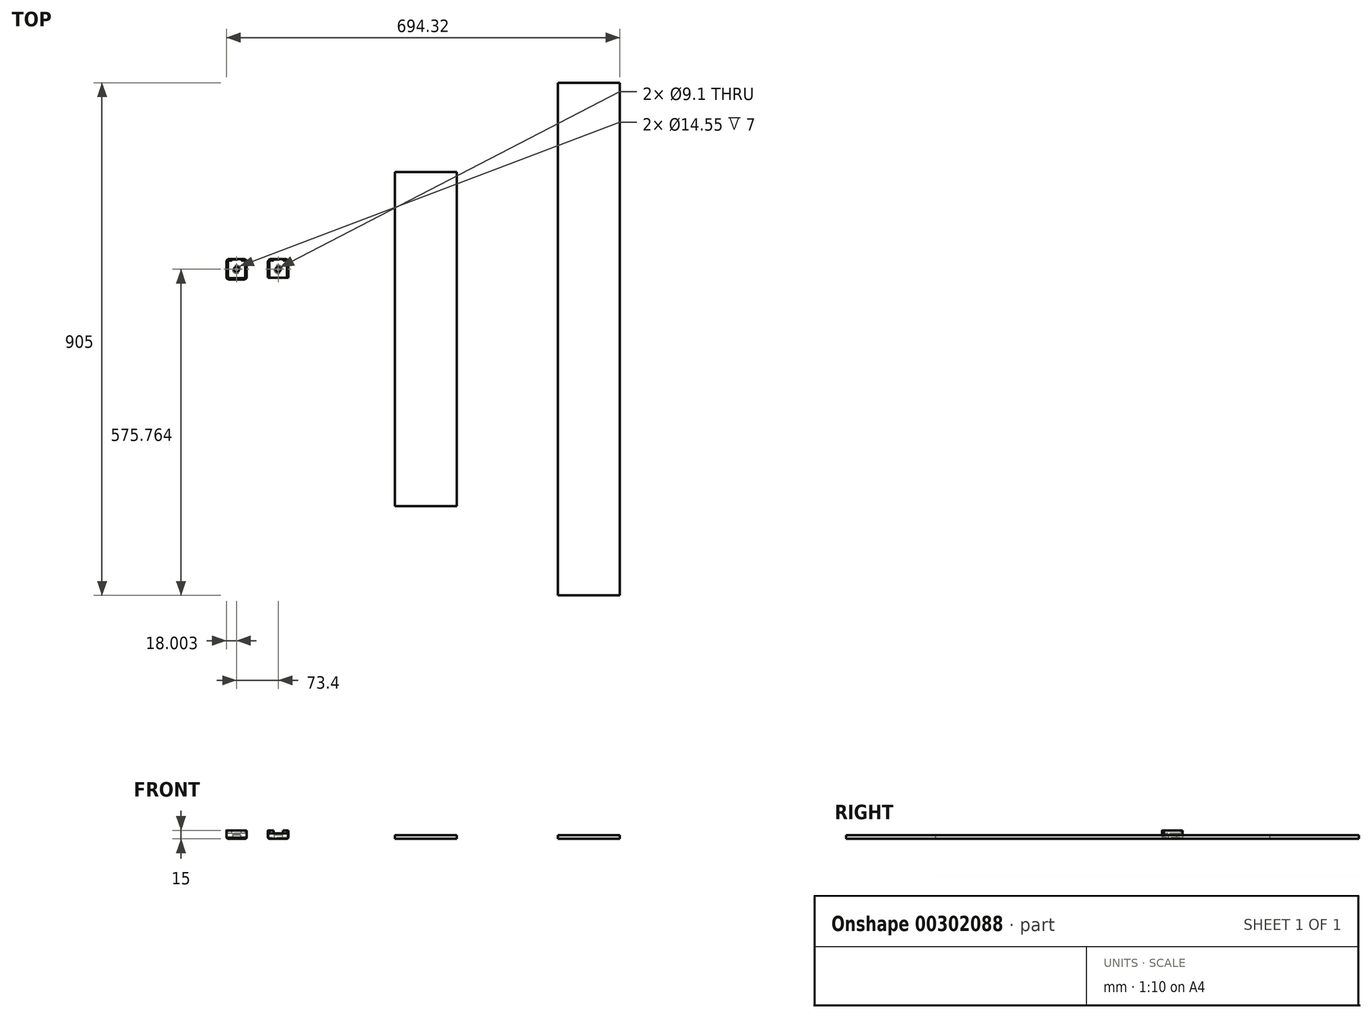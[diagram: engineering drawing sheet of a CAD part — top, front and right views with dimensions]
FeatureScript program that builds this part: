
annotation { "Feature Type Name" : "Feature", "Feature Type Description" : "" }
export const myFeature = defineFeature(function(context is Context, id is Id, definition is map)
    precondition{}
    {
        {
            var Q0;
            Q0=qCreatedBy(makeId("Top.planeOp"),FACE);
            var sketch = newSketch(context, id + "F0", { "sketchPlane" : qUnion([Q0])});
            skLineSegment(sketch, "E0.bottom", {"start": v(-54.5, 295) * mm, "end": v(54.5, 295) * mm});
            skLineSegment(sketch, "E0.top", {"start": v(-54.5, -295) * mm, "end": v(54.5, -295) * mm});
            skLineSegment(sketch, "E0.left", {"start": v(-54.5, 295) * mm, "end": v(-54.5, -295) * mm});
            skLineSegment(sketch, "E0.right", {"start": v(54.5, 295) * mm, "end": v(54.5, -295) * mm});
            skPoint(sketch, "E0.middle", {"position": v(0, 0) * mm});
            skLineSegment(sketch, "E1.bottom", {"start": v(233.4, 452.5) * mm, "end": v(342.4, 452.5) * mm});
            skLineSegment(sketch, "E1.top", {"start": v(233.4, -452.5) * mm, "end": v(342.4, -452.5) * mm});
            skLineSegment(sketch, "E1.left", {"start": v(233.4, 452.5) * mm, "end": v(233.4, -452.5) * mm});
            skLineSegment(sketch, "E1.right", {"start": v(342.4, 452.5) * mm, "end": v(342.4, -452.5) * mm});
            skPoint(sketch, "E1.middle", {"position": v(287.9, 0) * mm});
            skLineSegment(sketch, "E2.bottom", {"start": v(-351.92, 141.26) * mm, "end": v(-315.92, 141.26) * mm});
            skLineSegment(sketch, "E2.top", {"start": v(-351.92, 105.26) * mm, "end": v(-315.92, 105.26) * mm});
            skLineSegment(sketch, "E2.left", {"start": v(-351.92, 141.26) * mm, "end": v(-351.92, 105.26) * mm});
            skLineSegment(sketch, "E2.right", {"start": v(-315.92, 141.26) * mm, "end": v(-315.92, 105.26) * mm});
            skPoint(sketch, "E2.middle", {"position": v(-333.92, 123.26) * mm});
            skSolve(sketch);
        }
        {
            var Q0;
            Q0=makeQuery(id+"F0.imprint","IMPRINT",FACE,{"disambiguationData":[TD([[makeQuery(id+"F0.imprint","IMPRINT",EDGE,{"derivedFrom":sQuery(id+"F0.wireOp",EDGE,"E0.bottom")}),-1.0]])]});
            var Q1;
            Q1=makeQuery(id+"F0.imprint","IMPRINT",FACE,{"disambiguationData":[TD([[makeQuery(id+"F0.imprint","IMPRINT",EDGE,{"derivedFrom":sQuery(id+"F0.wireOp",EDGE,"E1.bottom")}),-1.0]])]});
            extrude(context, id + "F1", {"entities" : qUnion([Q0, Q1]), "depth" : 6.35 * mm});
        }
        {
            var Q0;
            Q0=makeQuery(id+"F0.imprint","IMPRINT",FACE,{"disambiguationData":[TD([[makeQuery(id+"F0.imprint","IMPRINT",EDGE,{"derivedFrom":sQuery(id+"F0.wireOp",EDGE,"E2.bottom")}),-1.0]])]});
            extrude(context, id + "F2", {"entities" : qUnion([Q0]), "depth" : 15 * mm});
        }
        {
            var Q0;
            Q0=makeQuery(id+"F2.opExtrude","CAP_FACE",FACE,{"disambiguationData":[OSD([sQuery(id+"F0.wireOp",EDGE,"E2.bottom"),sQuery(id+"F0.wireOp",EDGE,"E2.top"),sQuery(id+"F0.wireOp",EDGE,"E2.left"),sQuery(id+"F0.wireOp",EDGE,"E2.right")])],"isStart":false});
            var sketch = newSketch(context, id + "F3", { "sketchPlane" : qUnion([Q0])});
            skLineSegment(sketch, "E3.bottom", {"start": v(-318.42, 138.76) * mm, "end": v(-349.42, 138.76) * mm});
            skLineSegment(sketch, "E3.top", {"start": v(-318.42, 107.76) * mm, "end": v(-349.42, 107.76) * mm});
            skLineSegment(sketch, "E3.left", {"start": v(-318.42, 138.76) * mm, "end": v(-318.42, 107.76) * mm});
            skLineSegment(sketch, "E3.right", {"start": v(-349.42, 138.76) * mm, "end": v(-349.42, 107.76) * mm});
            skPoint(sketch, "E3.middle", {"position": v(-333.92, 123.26) * mm});
            skPoint(sketch, "E3.middle.positionSnap0", {"position": v(-351.92, 123.26) * mm});
            skPoint(sketch, "E3.middle.positionSnap1", {"position": v(-333.92, 141.26) * mm});
            skPoint(sketch, "E3.centerSnap0", {"position": v(-351.92, 123.26) * mm});
            skPoint(sketch, "E3.centerSnap1", {"position": v(-333.92, 141.26) * mm});
            skSolve(sketch);
        }
        {
            var Q0;
            Q0=makeQuery(id+"F3.imprint","IMPRINT",FACE,{"disambiguationData":[TD([[makeQuery(id+"F3.imprint","IMPRINT",EDGE,{"derivedFrom":sQuery(id+"F3.wireOp",EDGE,"E3.bottom")}),1.0]])]});
            extrude(context, id + "F4", {"entities" : qUnion([Q0]), "operationType" : NewBodyOperationType.REMOVE, "oppositeDirection" : true, "depth" : 5 * mm});
        }
        {
            var Q0;
            Q0=makeQuery(id+"F2.opExtrude","CAP_FACE",FACE,{"disambiguationData":[OSD([sQuery(id+"F0.wireOp",EDGE,"E2.bottom"),sQuery(id+"F0.wireOp",EDGE,"E2.top"),sQuery(id+"F0.wireOp",EDGE,"E2.left"),sQuery(id+"F0.wireOp",EDGE,"E2.right")])],"isStart":false});
            var sketch = newSketch(context, id + "F5", { "sketchPlane" : qUnion([Q0])});
            skLineSegment(sketch, "E4.bottom", {"start": v(-342.17, 141.26) * mm, "end": v(-325.67, 141.26) * mm});
            skLineSegment(sketch, "E4.top", {"start": v(-342.17, 138.76) * mm, "end": v(-325.67, 138.76) * mm});
            skLineSegment(sketch, "E4.left", {"start": v(-342.17, 141.26) * mm, "end": v(-342.17, 138.76) * mm});
            skLineSegment(sketch, "E4.right", {"start": v(-325.67, 141.26) * mm, "end": v(-325.67, 138.76) * mm});
            skPoint(sketch, "E5", {"position": v(-333.92, 141.26) * mm});
            skSolve(sketch);
        }
        {
            var Q0;
            Q0 = qSketchRegion(id + "F5", true);
            extrude(context, id + "F6", {"entities" : qUnion([Q0]), "operationType" : NewBodyOperationType.REMOVE, "oppositeDirection" : true, "depth" : 5 * mm});
        }
        {
            var Q0;
            Q0=sQuery(id+"F0.wireOp",VERTEX,"E2.middle");
            var Q1;
            Q1=makeQuery(id+"F2.opExtrude","SWEPT_BODY",BODY,{"disambiguationData":[OSD([sQuery(id+"F0.wireOp",EDGE,"E2.bottom"),sQuery(id+"F0.wireOp",EDGE,"E2.top"),sQuery(id+"F0.wireOp",EDGE,"E2.left"),sQuery(id+"F0.wireOp",EDGE,"E2.right")])]});
            hole(context, id + "F7", {"style" : HoleStyle.C_BORE, "endStyle" : HoleEndStyle.THROUGH, "oppositeDirection" : true, "holeDiameter" : 9.1 * mm, "cBoreDiameter" : 14.55 * mm, "cBoreDepth" : 7 * mm, "tappedDepth" : 12 * mm, "tapClearance" : 3, "locations" : qUnion([Q0]), "scope" : qUnion([Q1])});
        }
        {
            var Q0;
            Q0=makeQuery(id+"F2.opExtrude","SWEPT_EDGE",EDGE,{"disambiguationData":[OSD([sQuery(id+"F0.wireOp",EDGE,"E2.bottom"),sQuery(id+"F0.wireOp",EDGE,"E2.left")])]});
            var Q1;
            Q1=makeQuery(id+"F2.opExtrude","SWEPT_EDGE",EDGE,{"disambiguationData":[OSD([sQuery(id+"F0.wireOp",EDGE,"E2.top"),sQuery(id+"F0.wireOp",EDGE,"E2.left")])]});
            var Q2;
            Q2=makeQuery(id+"F2.opExtrude","SWEPT_EDGE",EDGE,{"disambiguationData":[OSD([sQuery(id+"F0.wireOp",EDGE,"E2.bottom"),sQuery(id+"F0.wireOp",EDGE,"E2.right")])]});
            var Q3;
            Q3=makeQuery(id+"F2.opExtrude","SWEPT_EDGE",EDGE,{"disambiguationData":[OSD([sQuery(id+"F0.wireOp",EDGE,"E2.top"),sQuery(id+"F0.wireOp",EDGE,"E2.right")])]});
            fillet(context, id + "F8", {"entities" : qUnion([Q0, Q1, Q2, Q3]), "radius" : 5 * mm, "tangentPropagation" : true, "allowEdgeOverflow" : false});
        }
        {
            var Q0;
            Q0=makeQuery(id+"F2.opExtrude","CAP_EDGE",EDGE,{"disambiguationData":[OSD([sQuery(id+"F0.wireOp",EDGE,"E2.top")])],"isStart":true});
            chamfer(context, id + "F9", {"entities" : qUnion([Q0]), "width" : 2 * mm, "tangentPropagation" : true});
        }
        {
            var Q0;
            Q0=makeQuery(id+"F2.opExtrude","SWEPT_BODY",BODY,{"disambiguationData":[OSD([sQuery(id+"F0.wireOp",EDGE,"E2.bottom"),sQuery(id+"F0.wireOp",EDGE,"E2.top"),sQuery(id+"F0.wireOp",EDGE,"E2.left"),sQuery(id+"F0.wireOp",EDGE,"E2.right")])]});
            transform(context, id + "F10", {"entities" : qUnion([Q0]), "transformType" : TransformType.TRANSLATION_3D, "dx" : 73.4 * mm, "dy" : 0 * mm, "dz" : 0 * mm, "makeCopy" : true});
        }
        {
            var Q0;
            Q0=makeQuery(id+"F10.opPattern","COPY",FACE,{"derivedFrom":makeQuery(id+"F4.boolean.opBoolean","COPY",FACE,{"derivedFrom":makeQuery(id+"F4.opExtrude","SWEPT_FACE",FACE,{"disambiguationData":[OSD([sQuery(id+"F3.wireOp",EDGE,"E3.top")])]})}),"instanceName":"1"});
            var sketch = newSketch(context, id + "F11", { "sketchPlane" : qUnion([Q0])});
            skLineSegment(sketch, "E6.0", {"start": v(245.02, 15) * mm, "end": v(276.02, 15) * mm});
            skLineSegment(sketch, "E7.0", {"start": v(245.02, 10) * mm, "end": v(276.02, 10) * mm});
            skLineSegment(sketch, "E8.0", {"start": v(245.02, 10) * mm, "end": v(245.02, 15) * mm});
            skSolve(sketch);
        }
        {
            var Q0;
            Q0=makeQuery(id+"F11.imprint","IMPRINT",FACE,{"disambiguationData":[TD([[makeQuery(id+"F11.imprint","IMPRINT",EDGE,{"derivedFrom":sQuery(id+"F11.wireOp",EDGE,"E6.0")}),-1.0]])]});
            extrude(context, id + "F12", {"entities" : qUnion([Q0]), "operationType" : NewBodyOperationType.REMOVE, "oppositeDirection" : true, "depth" : 25 * mm});
        }
        {
            var Q0;
            Q0=makeQuery(id+"F12.boolean.opBoolean","INTERSECT",EDGE,{"derivedFrom":[makeQuery(id+"F10.opPattern","COPY",FACE,{"derivedFrom":makeQuery(id+"F8.opFillet","BLEND_FACE",FACE,{"disambiguationData":[OSD([sQuery(id+"F0.wireOp",EDGE,"E2.top"),sQuery(id+"F0.wireOp",EDGE,"E2.right")])]}),"instanceName":"1"}),makeQuery(id+"F12.opExtrude","SWEPT_FACE",FACE,{"disambiguationData":[OSD([sQuery(id+"F11.wireOp",EDGE,"E8.0")])]})]});
            var Q1;
            Q1=makeQuery(id+"F12.boolean.opBoolean","INTERSECT",EDGE,{"derivedFrom":[makeQuery(id+"F10.opPattern","COPY",FACE,{"derivedFrom":makeQuery(id+"F8.opFillet","BLEND_FACE",FACE,{"disambiguationData":[OSD([sQuery(id+"F0.wireOp",EDGE,"E2.top"),sQuery(id+"F0.wireOp",EDGE,"E2.left")])]}),"instanceName":"1"}),makeQuery(id+"F12.opExtrude","SWEPT_FACE",FACE,{"disambiguationData":[OSD([sQuery(id+"F3.wireOp",EDGE,"E3.top"),sQuery(id+"F3.wireOp",EDGE,"E3.right")])]})]});
            fillet(context, id + "F13", {"entities" : qUnion([Q0, Q1]), "radius" : 0.5 * mm, "tangentPropagation" : true, "allowEdgeOverflow" : false});
        }
        {
            var Q0;
            Q0=makeQuery(id+"F12.boolean.opBoolean","MERGE",FACE,{"derivedFrom":[makeQuery(id+"F10.opPattern","COPY",FACE,{"derivedFrom":makeQuery(id+"F6.boolean.opBoolean","MERGE",FACE,{"derivedFrom":[makeQuery(id+"F4.boolean.opBoolean","COPY",FACE,{"derivedFrom":makeQuery(id+"F4.opExtrude","CAP_FACE",FACE,{"disambiguationData":[OSD([sQuery(id+"F3.wireOp",EDGE,"E3.bottom"),sQuery(id+"F3.wireOp",EDGE,"E3.top"),sQuery(id+"F3.wireOp",EDGE,"E3.left"),sQuery(id+"F3.wireOp",EDGE,"E3.right")])],"isStart":false})}),makeQuery(id+"F6.opExtrude","CAP_FACE",FACE,{"disambiguationData":[OSD([sQuery(id+"F5.wireOp",EDGE,"E4.bottom"),sQuery(id+"F5.wireOp",EDGE,"E4.top"),sQuery(id+"F5.wireOp",EDGE,"E4.left"),sQuery(id+"F5.wireOp",EDGE,"E4.right")])],"isStart":false})]}),"instanceName":"1"}),makeQuery(id+"F12.opExtrude","SWEPT_FACE",FACE,{"disambiguationData":[OSD([sQuery(id+"F11.wireOp",EDGE,"E7.0")])]})]});
            var sketch = newSketch(context, id + "F14", { "sketchPlane" : qUnion([Q0])});
            skCircle(sketch, "E9.0", {"center": v(-260.52, 123.26) * mm, "radius": 4.55 * mm});
            skLineSegment(sketch, "E10.bottom", {"start": v(-275.52, 138.26) * mm, "end": v(-245.52, 138.26) * mm, "construction": true});
            skLineSegment(sketch, "E10.top", {"start": v(-275.52, 108.26) * mm, "end": v(-245.52, 108.26) * mm, "construction": true});
            skLineSegment(sketch, "E10.left", {"start": v(-275.52, 138.26) * mm, "end": v(-275.52, 108.26) * mm, "construction": true});
            skLineSegment(sketch, "E10.right", {"start": v(-245.52, 138.26) * mm, "end": v(-245.52, 108.26) * mm, "construction": true});
            skLineSegment(sketch, "E11.0", {"start": v(-247.52, 105.26) * mm, "end": v(-273.52, 105.26) * mm});
            skArc(sketch, "E12.0", {"start": v(-247.52, 105.26) * mm, "mid": v(-245.73, 105.6) * mm, "end": v(-244.18, 106.54) * mm});
            skArc(sketch, "E13.0", {"start": v(-244.18, 106.54) * mm, "mid": v(-243.47, 107.33) * mm, "end": v(-242.93, 108.26) * mm});
            skArc(sketch, "E14.0", {"start": v(-276.85, 106.54) * mm, "mid": v(-275.3, 105.6) * mm, "end": v(-273.52, 105.26) * mm});
            skArc(sketch, "E15.0", {"start": v(-278.1, 108.26) * mm, "mid": v(-276.26, 106.08) * mm, "end": v(-273.52, 105.26) * mm});
            skLineSegment(sketch, "E16", {"start": v(-278.1, 108.26) * mm, "end": v(-242.93, 108.26) * mm});
            skPoint(sketch, "E17.orphan", {"position": v(-278.52, 110.26) * mm});
            skPoint(sketch, "E18.orphan", {"position": v(-242.52, 110.26) * mm});
            skSolve(sketch);
        }
        {
            var Q0;
            {var subQ1=sQuery(id+"F3.wireOp",EDGE,"E3.left");var subQ2=makeQuery(id+"F4.boolean.opBoolean","COPY",FACE,{"derivedFrom":makeQuery(id+"F4.opExtrude","SWEPT_FACE",FACE,{"disambiguationData":[OSD([subQ1])]})});var subQ4=sQuery(id+"F0.wireOp",EDGE,"E2.right");var subQ5=sQuery(id+"F0.wireOp",EDGE,"E2.top");var subQ6=sQuery(id+"F0.wireOp",EDGE,"E2.bottom");var subQ7=makeQuery(id+"F2.opExtrude","CAP_FACE",FACE,{"disambiguationData":[OSD([subQ6,subQ5,sQuery(id+"F0.wireOp",EDGE,"E2.left"),subQ4])],"isStart":false});Q0=makeQuery(id+"F12.boolean.opBoolean","SPLIT",FACE,{"disambiguationData":[TD([makeQuery(id+"F10.opPattern","COPY",FACE,{"derivedFrom":subQ2,"instanceName":"1"})])],"derivedFrom":makeQuery(id+"F10.opPattern","COPY",FACE,{"derivedFrom":subQ7,"instanceName":"1"})});}
            var sketch = newSketch(context, id + "F15", { "sketchPlane" : qUnion([Q0])});
            skLineSegment(sketch, "E19.0", {"start": v(-278.1, 108.26) * mm, "end": v(-242.93, 108.26) * mm});
            skArc(sketch, "E20.0", {"start": v(-278.1, 108.26) * mm, "mid": v(-276.26, 106.08) * mm, "end": v(-273.52, 105.26) * mm});
            skLineSegment(sketch, "E21.0", {"start": v(-247.52, 105.26) * mm, "end": v(-273.52, 105.26) * mm});
            skArc(sketch, "E22.0", {"start": v(-247.52, 105.26) * mm, "mid": v(-245.73, 105.6) * mm, "end": v(-244.18, 106.54) * mm});
            skArc(sketch, "E23.0", {"start": v(-244.18, 106.54) * mm, "mid": v(-243.47, 107.33) * mm, "end": v(-242.93, 108.26) * mm});
            skSolve(sketch);
        }
        {
            var Q0;
            {var subQ16=sQuery(id+"F15.wireOp",EDGE,"E20.0");Q0=makeQuery(id+"F15.imprint","IMPRINT",FACE,{"disambiguationData":[TD([[makeQuery(id+"F15.imprint","IMPRINT",EDGE,{"derivedFrom":subQ16}),1.0]])]});}
            var Q1;
            {var subQ0=sQuery(id+"F15.wireOp",EDGE,"E23.0");Q1=makeQuery(id+"F15.imprint","IMPRINT",FACE,{"disambiguationData":[TD([[makeQuery(id+"F15.imprint","IMPRINT",EDGE,{"derivedFrom":subQ0}),1.0]])]});}
            var Q2;
            Q2=makeQuery(id+"F10.opPattern","COPY",FACE,{"derivedFrom":makeQuery(id+"F2.opExtrude","CAP_FACE",FACE,{"disambiguationData":[OSD([sQuery(id+"F0.wireOp",EDGE,"E2.bottom"),sQuery(id+"F0.wireOp",EDGE,"E2.top"),sQuery(id+"F0.wireOp",EDGE,"E2.left"),sQuery(id+"F0.wireOp",EDGE,"E2.right")])],"isStart":true}),"instanceName":"1"});
            extrude(context, id + "F16", {"entities" : qUnion([Q0, Q1]), "operationType" : NewBodyOperationType.REMOVE, "endBound" : BoundingType.UP_TO_SURFACE, "oppositeDirection" : true, "endBoundEntityFace" : qUnion([Q2]), "depth" : 25 * mm});
        }
        {
            var Q0;
            Q0=makeQuery(id+"F16.boolean.opBoolean","COPY",EDGE,{"derivedFrom":makeQuery(id+"F16.opExtrude","SWEPT_EDGE",EDGE,{"disambiguationData":[OSD([sQuery(id+"F15.wireOp",EDGE,"E19.0"),sQuery(id+"F15.wireOp",EDGE,"E20.0")])]})});
            var Q1;
            Q1=makeQuery(id+"F16.boolean.opBoolean","COPY",EDGE,{"derivedFrom":makeQuery(id+"F16.opExtrude","SWEPT_EDGE",EDGE,{"disambiguationData":[OSD([sQuery(id+"F0.wireOp",EDGE,"E2.bottom"),sQuery(id+"F0.wireOp",EDGE,"E2.top"),sQuery(id+"F0.wireOp",EDGE,"E2.left"),sQuery(id+"F0.wireOp",EDGE,"E2.right"),sQuery(id+"F15.wireOp",EDGE,"E19.0"),sQuery(id+"F15.wireOp",EDGE,"E23.0")])]})});
            var Q2;
            Q2=makeQuery(id+"F16.boolean.opBoolean","INTERSECT",EDGE,{"derivedFrom":[makeQuery(id+"F12.boolean.opBoolean","MERGE",FACE,{"derivedFrom":[makeQuery(id+"F10.opPattern","COPY",FACE,{"derivedFrom":makeQuery(id+"F4.boolean.opBoolean","COPY",FACE,{"derivedFrom":makeQuery(id+"F4.opExtrude","SWEPT_FACE",FACE,{"disambiguationData":[OSD([sQuery(id+"F3.wireOp",EDGE,"E3.left")])]})}),"instanceName":"1"}),makeQuery(id+"F12.opExtrude","SWEPT_FACE",FACE,{"disambiguationData":[OSD([sQuery(id+"F11.wireOp",EDGE,"E8.0")])]})]}),makeQuery(id+"F16.opExtrude","SWEPT_FACE",FACE,{"disambiguationData":[OSD([sQuery(id+"F15.wireOp",EDGE,"E19.0")])]})]});
            var Q3;
            {var subQ0=sQuery(id+"F3.wireOp",EDGE,"E3.right");Q3=makeQuery(id+"F16.boolean.opBoolean","INTERSECT",EDGE,{"derivedFrom":[makeQuery(id+"F12.boolean.opBoolean","MERGE",FACE,{"derivedFrom":[makeQuery(id+"F10.opPattern","COPY",FACE,{"derivedFrom":makeQuery(id+"F4.boolean.opBoolean","COPY",FACE,{"derivedFrom":makeQuery(id+"F4.opExtrude","SWEPT_FACE",FACE,{"disambiguationData":[OSD([subQ0])]})}),"instanceName":"1"}),makeQuery(id+"F12.opExtrude","SWEPT_FACE",FACE,{"disambiguationData":[OSD([sQuery(id+"F3.wireOp",EDGE,"E3.top"),subQ0])]})]}),makeQuery(id+"F16.opExtrude","SWEPT_FACE",FACE,{"disambiguationData":[OSD([sQuery(id+"F15.wireOp",EDGE,"E19.0")])]})]});}
            fillet(context, id + "F17", {"entities" : qUnion([Q0, Q1, Q2, Q3]), "radius" : 1 * mm, "tangentPropagation" : true, "allowEdgeOverflow" : false});
        }
    });
